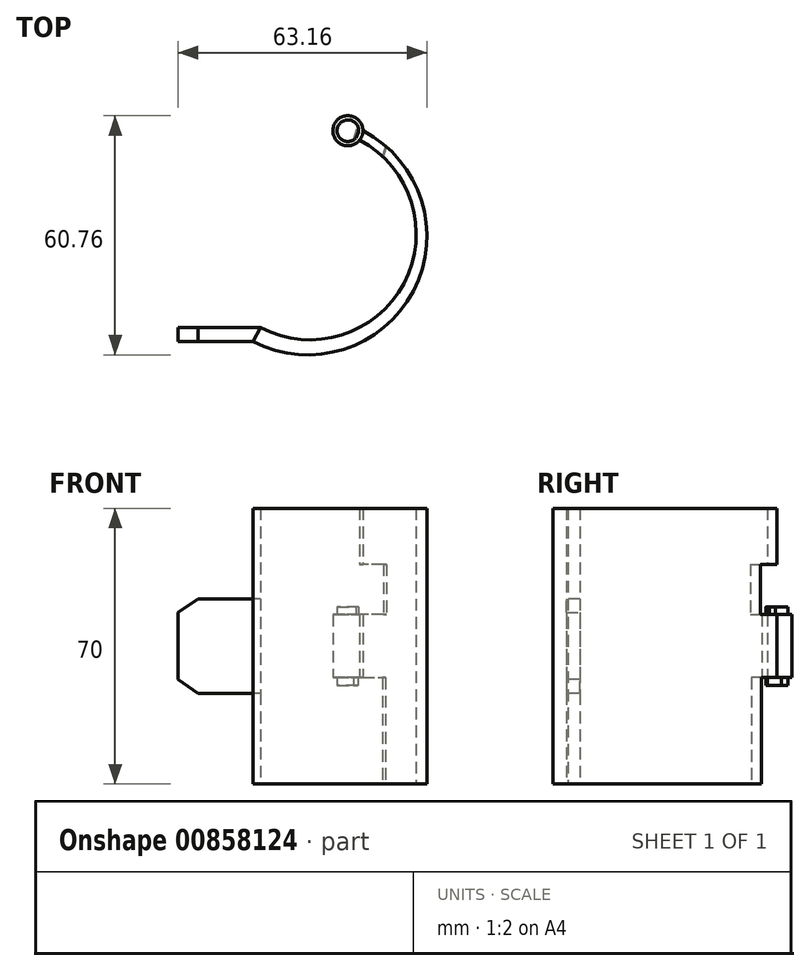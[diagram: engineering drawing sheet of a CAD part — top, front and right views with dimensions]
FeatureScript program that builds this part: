
annotation { "Feature Type Name" : "Feature", "Feature Type Description" : "" }
export const myFeature = defineFeature(function(context is Context, id is Id, definition is map)
    precondition{}
    {
        {
            var Q0;
            Q0=qCreatedBy(makeId("Top.planeOp"),FACE);
            var sketch = newSketch(context, id + "F0", { "sketchPlane" : qUnion([Q0])});
            skCircle(sketch, "E0", {"center": v(0, 0) * mm, "radius": 2.75 * mm});
            skCircle(sketch, "E1", {"center": v(0, 0) * mm, "radius": 3.82 * mm});
            skArc(sketch, "E2", {"start": v(-22.18, -50) * mm, "mid": v(14.22, -38.77) * mm, "end": v(3, -2.37) * mm});
            skArc(sketch, "E3", {"start": v(-24.06, -53.53) * mm, "mid": v(16.65, -40.7) * mm, "end": v(3.82, 0) * mm});
            skLineSegment(sketch, "E4", {"start": v(-22.18, -50) * mm, "end": v(-24.06, -53.53) * mm});
            skLineSegment(sketch, "E5", {"start": v(-22.18, -50) * mm, "end": v(-43.1, -50) * mm});
            skLineSegment(sketch, "E6", {"start": v(-24.06, -53.53) * mm, "end": v(-43.1, -53.53) * mm});
            skLineSegment(sketch, "E7", {"start": v(-43.1, -53.53) * mm, "end": v(-43.1, -50) * mm});
            skSolve(sketch);
        }
        {
            var Q0;
            {var subQ0=sQuery(id+"F0.wireOp",EDGE,"E2");Q0=makeQuery(id+"F0.imprint","IMPRINT",FACE,{"disambiguationData":[TD([[makeQuery(id+"F0.imprint","IMPRINT",EDGE,{"derivedFrom":subQ0}),-1.0]])]});}
            extrude(context, id + "F1", {"entities" : qUnion([Q0]), "depth" : 43 * mm, "offsetDistance" : 25 * mm, "hasSecondDirection" : true, "secondDirectionOppositeDirection" : true, "secondDirectionDepth" : 10 * mm});
        }
        {
            var Q0;
            Q0=makeQuery(id+"F0.imprint","IMPRINT",FACE,{"disambiguationData":[TD([[makeQuery(id+"F0.imprint","IMPRINT",EDGE,{"derivedFrom":sQuery(id+"F0.wireOp",EDGE,"E4")}),-1.0]])]});
            extrude(context, id + "F2", {"entities" : qUnion([Q0]), "operationType" : NewBodyOperationType.ADD, "depth" : 20 * mm, "offsetDistance" : 25 * mm, "hasSecondDirection" : true, "secondDirectionOppositeDirection" : true, "secondDirectionDepth" : 4 * mm});
        }
        {
            var Q0;
            Q0=makeQuery(id+"F2.opExtrude","CAP_EDGE",EDGE,{"disambiguationData":[OSD([sQuery(id+"F0.wireOp",EDGE,"E7")])],"isStart":false});
            var Q1;
            Q1=makeQuery(id+"F2.opExtrude","CAP_EDGE",EDGE,{"disambiguationData":[OSD([sQuery(id+"F0.wireOp",EDGE,"E7")])],"isStart":true});
            chamfer(context, id + "F3", {"entities" : qUnion([Q0, Q1]), "chamferType" : ChamferType.OFFSET_ANGLE, "width" : 3.5 * mm, "oppositeDirection" : false, "angle" : 55 * degree, "tangentPropagation" : true});
        }
        {
            var Q0;
            Q0=makeQuery(id+"F0.imprint","IMPRINT",FACE,{"disambiguationData":[TD([[makeQuery(id+"F0.imprint","IMPRINT",EDGE,{"derivedFrom":sQuery(id+"F0.wireOp",EDGE,"E0")}),-1.0]])]});
            extrude(context, id + "F4", {"entities" : qUnion([Q0]), "operationType" : NewBodyOperationType.ADD, "depth" : 16 * mm, "offsetDistance" : 25 * mm});
        }
        {
            var Q0;
            Q0=makeQuery(id+"F0.imprint","IMPRINT",FACE,{"disambiguationData":[TD([[makeQuery(id+"F0.imprint","IMPRINT",EDGE,{"derivedFrom":sQuery(id+"F0.wireOp",EDGE,"E0")}),1.0]])]});
            extrude(context, id + "F5", {"entities" : qUnion([Q0]), "operationType" : NewBodyOperationType.ADD, "depth" : 18 * mm, "offsetDistance" : 25 * mm, "hasSecondDirection" : true, "secondDirectionOppositeDirection" : true, "secondDirectionDepth" : 2 * mm});
        }
        {
            var Q0;
            Q0=makeQuery(id+"F4.opExtrude","CAP_FACE",FACE,{"disambiguationData":[OSD([sQuery(id+"F0.wireOp",EDGE,"E0"),sQuery(id+"F0.wireOp",EDGE,"E1")])],"isStart":true});
            var sketch = newSketch(context, id + "F6", { "sketchPlane" : qUnion([Q0])});
            skLineSegment(sketch, "E8", {"start": v(3.96, -1) * mm, "end": v(1.59, 6.2) * mm});
            skLineSegment(sketch, "E9", {"start": v(1.59, 6.2) * mm, "end": v(0.27, 5.77) * mm});
            skLineSegment(sketch, "E10", {"start": v(0.27, 5.77) * mm, "end": v(3.96, -1) * mm});
            skSolve(sketch);
        }
        {
            var Q0;
            {var subQ0=sQuery(id+"F6.wireOp",EDGE,"E9");Q0=makeQuery(id+"F6.imprint","IMPRINT",FACE,{"disambiguationData":[TD([[makeQuery(id+"F6.imprint","IMPRINT",EDGE,{"derivedFrom":subQ0}),1.0]])]});}
            var Q1;
            {var subQ0=sQuery(id+"F6.wireOp",EDGE,"E8");var subQ1=sQuery(id+"F0.wireOp",EDGE,"E1");var subQ2=makeQuery(id+"F4.boolean.opBoolean","SPLIT",EDGE,{"disambiguationData":[topologyDisambiguationEdgeConnected([makeQuery(id+"F4.opExtrude","SWEPT_FACE",FACE,{"disambiguationData":[OSD([subQ1])]})])],"derivedFrom":makeQuery(id+"F4.opExtrude","CAP_EDGE",EDGE,{"disambiguationData":[OSD([subQ1])],"isStart":true})});var subQ3=makeQuery(id+"F6.imprint","INTERSECT",VERTEX,{"disambiguationData":[OD(0.0)],"derivedFrom":[subQ2,subQ0]});Q1=makeQuery(id+"F6.imprint","IMPRINT",FACE,{"disambiguationData":[TD([[makeQuery(id+"F6.imprint","IMPRINT",EDGE,{"disambiguationData":[TD([[subQ3,-1.0]])],"derivedFrom":subQ0}),1.0]])]});}
            var Q2;
            {var subQ0=sQuery(id+"F6.wireOp",EDGE,"E10");var subQ1=sQuery(id+"F6.wireOp",EDGE,"E8");var subQ2=makeQuery(id+"F6.imprint","INTERSECT",VERTEX,{"derivedFrom":[subQ1,subQ0]});Q2=makeQuery(id+"F6.imprint","IMPRINT",FACE,{"disambiguationData":[TD([[makeQuery(id+"F6.imprint","IMPRINT",EDGE,{"disambiguationData":[TD([[subQ2,-1.0]])],"derivedFrom":subQ1}),1.0]])]});}
            extrude(context, id + "F7", {"entities" : qUnion([Q0, Q1, Q2]), "operationType" : NewBodyOperationType.ADD, "depth" : 25 * mm, "offsetDistance" : 25 * mm});
        }
        {
            var Q0;
            Q0=makeQuery(id+"F7.opExtrude","SWEPT_FACE",FACE,{"disambiguationData":[OSD([sQuery(id+"F6.wireOp",EDGE,"E8")])]});
            extrude(context, id + "F8", {"entities" : qUnion([Q0]), "operationType" : NewBodyOperationType.REMOVE, "depth" : 6.9 * mm, "offsetDistance" : 25 * mm});
        }
        {
            var Q0;
            Q0=makeQuery(id+"F4.opExtrude","CAP_FACE",FACE,{"disambiguationData":[OSD([sQuery(id+"F0.wireOp",EDGE,"E0"),sQuery(id+"F0.wireOp",EDGE,"E1")])],"isStart":false});
            var sketch = newSketch(context, id + "F9", { "sketchPlane" : qUnion([Q0])});
            skLineSegment(sketch, "E11", {"start": v(1.68, -5.84) * mm, "end": v(4.28, 1.9) * mm});
            skLineSegment(sketch, "E12", {"start": v(4.28, 1.9) * mm, "end": v(0.42, -5.25) * mm});
            skLineSegment(sketch, "E13", {"start": v(0.42, -5.25) * mm, "end": v(1.68, -5.84) * mm});
            skSolve(sketch);
        }
        {
            var Q0;
            {var subQ0=sQuery(id+"F9.wireOp",EDGE,"E13");Q0=makeQuery(id+"F9.imprint","IMPRINT",FACE,{"disambiguationData":[TD([[makeQuery(id+"F9.imprint","IMPRINT",EDGE,{"derivedFrom":subQ0}),1.0]])]});}
            var Q1;
            {var subQ0=sQuery(id+"F9.wireOp",EDGE,"E11");var subQ1=sQuery(id+"F0.wireOp",EDGE,"E1");var subQ2=makeQuery(id+"F4.boolean.opBoolean","SPLIT",EDGE,{"disambiguationData":[topologyDisambiguationEdgeConnected([makeQuery(id+"F4.opExtrude","SWEPT_FACE",FACE,{"disambiguationData":[OSD([subQ1])]})])],"derivedFrom":makeQuery(id+"F4.opExtrude","CAP_EDGE",EDGE,{"disambiguationData":[OSD([subQ1])],"isStart":false})});var subQ3=makeQuery(id+"F9.imprint","INTERSECT",VERTEX,{"disambiguationData":[OD(0.0)],"derivedFrom":[subQ2,subQ0]});Q1=makeQuery(id+"F9.imprint","IMPRINT",FACE,{"disambiguationData":[TD([[makeQuery(id+"F9.imprint","IMPRINT",EDGE,{"disambiguationData":[TD([[subQ3,-1.0]])],"derivedFrom":subQ0}),1.0]])]});}
            var Q2;
            {var subQ0=sQuery(id+"F9.wireOp",EDGE,"E12");var subQ1=sQuery(id+"F9.wireOp",EDGE,"E11");var subQ2=makeQuery(id+"F9.imprint","INTERSECT",VERTEX,{"derivedFrom":[subQ1,subQ0]});Q2=makeQuery(id+"F9.imprint","IMPRINT",FACE,{"disambiguationData":[TD([[makeQuery(id+"F9.imprint","IMPRINT",EDGE,{"disambiguationData":[TD([[subQ2,1.0]])],"derivedFrom":subQ1}),1.0]])]});}
            extrude(context, id + "F10", {"entities" : qUnion([Q0, Q1, Q2]), "operationType" : NewBodyOperationType.ADD, "depth" : 12.8 * mm, "offsetDistance" : 25 * mm});
        }
        {
            var Q0;
            Q0=makeQuery(id+"F10.opExtrude","SWEPT_FACE",FACE,{"disambiguationData":[OSD([sQuery(id+"F9.wireOp",EDGE,"E11")])]});
            extrude(context, id + "F11", {"entities" : qUnion([Q0]), "operationType" : NewBodyOperationType.REMOVE, "depth" : 7.2 * mm, "offsetDistance" : 25 * mm});
        }
        {
            var Q0;
            Q0=makeQuery(id+"F10.opExtrude","SWEPT_FACE",FACE,{"disambiguationData":[OSD([sQuery(id+"F9.wireOp",EDGE,"E13")])]});
            extrude(context, id + "F12", {"entities" : qUnion([Q0]), "operationType" : NewBodyOperationType.REMOVE, "oppositeDirection" : true, "depth" : 25 * mm, "offsetDistance" : 25 * mm});
        }
        {
            var Q0;
            Q0=makeQuery(id+"F7.opExtrude","SWEPT_FACE",FACE,{"disambiguationData":[OSD([sQuery(id+"F6.wireOp",EDGE,"E9")])]});
            extrude(context, id + "F13", {"entities" : qUnion([Q0]), "operationType" : NewBodyOperationType.REMOVE, "oppositeDirection" : true, "depth" : 25 * mm, "offsetDistance" : 25 * mm});
        }
        {
            var Q0;
            Q0=makeQuery(id+"F1.opExtrude","CAP_FACE",FACE,{"disambiguationData":[OSD([sQuery(id+"F0.wireOp",EDGE,"E1"),sQuery(id+"F0.wireOp",EDGE,"E2"),sQuery(id+"F0.wireOp",EDGE,"E3"),sQuery(id+"F0.wireOp",EDGE,"E4")])],"isStart":true});
            extrude(context, id + "F14", {"entities" : qUnion([Q0]), "operationType" : NewBodyOperationType.ADD, "depth" : 17 * mm, "offsetDistance" : 25 * mm});
        }
    });
